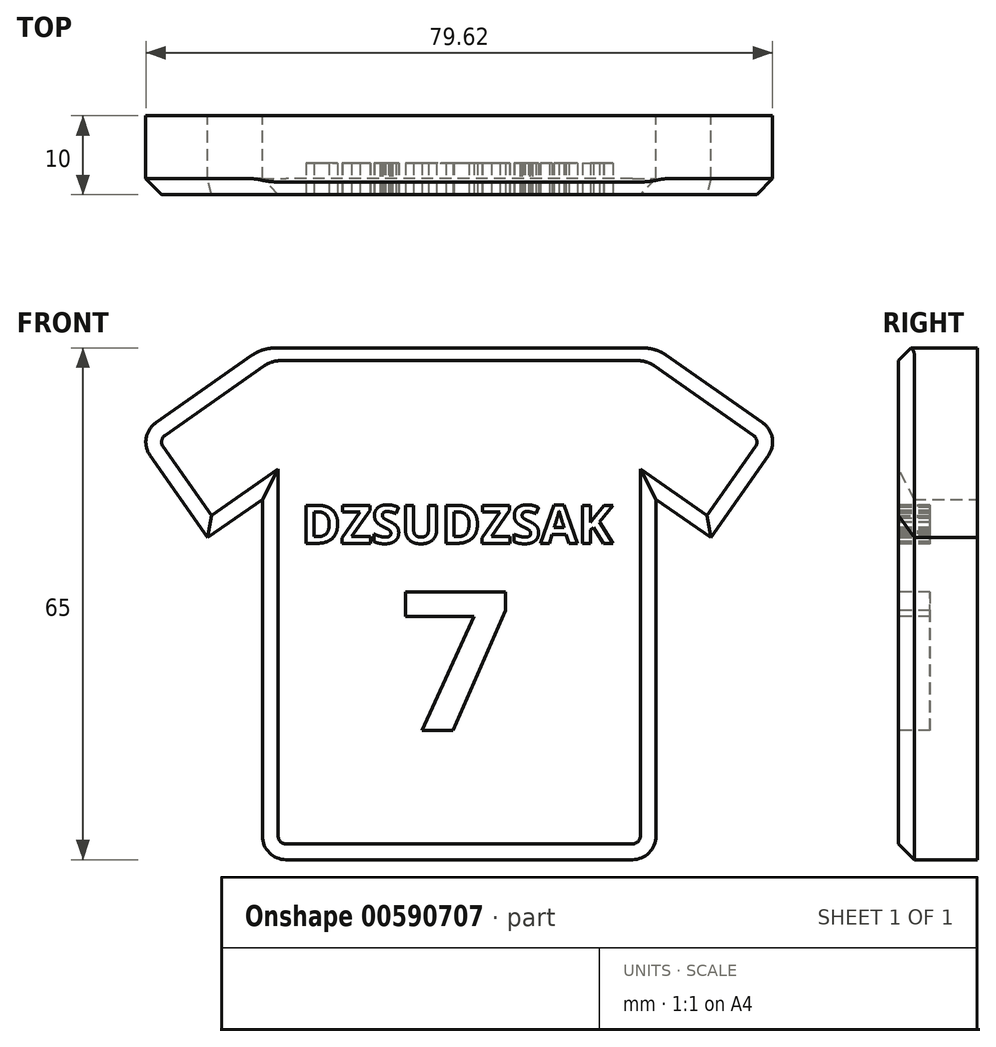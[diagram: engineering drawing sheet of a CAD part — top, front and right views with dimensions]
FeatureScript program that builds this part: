
annotation { "Feature Type Name" : "Feature", "Feature Type Description" : "" }
export const myFeature = defineFeature(function(context is Context, id is Id, definition is map)
    precondition{}
    {
        {
            var Q0;
            Q0=qCreatedBy(makeId("Front.planeOp"),FACE);
            var sketch = newSketch(context, id + "F0", { "sketchPlane" : qUnion([Q0])});
            skLineSegment(sketch, "E0.bottom", {"start": v(0, 36.36) * mm, "end": v(-25, 36.36) * mm});
            skLineSegment(sketch, "E0.top", {"start": v(0, -28.64) * mm, "end": v(-22, -28.64) * mm});
            skLineSegment(sketch, "E0.left", {"start": v(0, 36.36) * mm, "end": v(0, -28.64) * mm});
            skLineSegment(sketch, "E0.right", {"start": v(-25, 36.36) * mm, "end": v(-25, -25.64) * mm});
            skPoint(sketch, "E1.visualSharp", {"position": v(-25, -28.64) * mm});
            skArc(sketch, "E1.filletArc", {"start": v(-25, -25.64) * mm, "mid": v(-24.12, -27.76) * mm, "end": v(-22, -28.64) * mm});
            skArc(sketch, "E2.MirrorCS", {"start": v(25, -25.64) * mm, "mid": v(24.12, -27.76) * mm, "end": v(22, -28.64) * mm});
            skLineSegment(sketch, "E3.MirrorCS", {"start": v(25, 36.36) * mm, "end": v(25, -25.64) * mm});
            skLineSegment(sketch, "E4.MirrorCS", {"start": v(0, 36.36) * mm, "end": v(25, 36.36) * mm});
            skPoint(sketch, "E5.MirrorP", {"position": v(25, -28.64) * mm});
            skLineSegment(sketch, "E6.MirrorCS", {"start": v(0, -28.64) * mm, "end": v(22, -28.64) * mm});
            skLineSegment(sketch, "E7.bottom", {"start": v(25, 36.36) * mm, "end": v(41, 25.16) * mm});
            skLineSegment(sketch, "E7.top", {"start": v(15.98, 23.47) * mm, "end": v(31.97, 12.27) * mm});
            skLineSegment(sketch, "E7.left", {"start": v(25, 36.36) * mm, "end": v(15.98, 23.47) * mm});
            skLineSegment(sketch, "E7.right", {"start": v(41, 25.16) * mm, "end": v(31.97, 12.27) * mm});
            skLineSegment(sketch, "E8.MirrorCS", {"start": v(-25, 36.36) * mm, "end": v(-24.97, 36.32) * mm});
            skPoint(sketch, "E9.orphan", {"position": v(-15.98, 23.47) * mm});
            skLineSegment(sketch, "E10.MirrorCS", {"start": v(-24.97, 36.32) * mm, "end": v(-15.98, 23.47) * mm});
            skLineSegment(sketch, "E11.MirrorCS", {"start": v(-15.98, 23.47) * mm, "end": v(-31.97, 12.27) * mm});
            skLineSegment(sketch, "E12.MirrorCS", {"start": v(-25, 36.36) * mm, "end": v(-41, 25.16) * mm});
            skLineSegment(sketch, "E13", {"start": v(-41, 25.16) * mm, "end": v(-31.97, 12.27) * mm});
            skPoint(sketch, "E14.orphan", {"position": v(-25, 36.36) * mm});
            skSolve(sketch);
        }
        {
            var Q0;
            {var subQ0=sQuery(id+"F0.wireOp",EDGE,"E7.left");Q0=makeQuery(id+"F0.imprint","IMPRINT",FACE,{"disambiguationData":[TD([[makeQuery(id+"F0.imprint","IMPRINT",EDGE,{"derivedFrom":subQ0}),1.0]])]});}
            var Q1;
            {var subQ0=sQuery(id+"F0.wireOp",EDGE,"E7.bottom");Q1=makeQuery(id+"F0.imprint","IMPRINT",FACE,{"disambiguationData":[TD([[makeQuery(id+"F0.imprint","IMPRINT",EDGE,{"derivedFrom":subQ0}),-1.0]])]});}
            var Q2;
            Q2=makeQuery(id+"F0.imprint","IMPRINT",FACE,{"disambiguationData":[TD([[makeQuery(id+"F0.imprint","IMPRINT",EDGE,{"derivedFrom":sQuery(id+"F0.wireOp",EDGE,"E0.left")}),1.0]])]});
            var Q3;
            {var subQ0=sQuery(id+"F0.wireOp",EDGE,"E12.MirrorCS");Q3=makeQuery(id+"F0.imprint","IMPRINT",FACE,{"disambiguationData":[TD([[makeQuery(id+"F0.imprint","IMPRINT",EDGE,{"derivedFrom":subQ0}),1.0]])]});}
            var Q4;
            Q4=makeQuery(id+"F0.imprint","IMPRINT",FACE,{"disambiguationData":[TD([[makeQuery(id+"F0.imprint","IMPRINT",EDGE,{"derivedFrom":sQuery(id+"F0.wireOp",EDGE,"E0.top")}),-1.0]])]});
            var Q5;
            {var subQ0=sQuery(id+"F0.wireOp",EDGE,"961204d5-9f19-48ca-a84b-a6f01696a6780.MirrorCS");var subQ1=sQuery(id+"F0.wireOp",EDGE,"E0.right");var subQ2=makeQuery(id+"F0.imprint","INTERSECT",VERTEX,{"derivedFrom":[subQ1,subQ0]});Q5=makeQuery(id+"F0.imprint","IMPRINT",FACE,{"disambiguationData":[TD([[makeQuery(id+"F0.imprint","IMPRINT",EDGE,{"disambiguationData":[TD([[subQ2,-1.0]])],"derivedFrom":subQ1}),1.0]])]});}
            var Q6;
            {var subQ0=sQuery(id+"F0.wireOp",EDGE,"718d626f-1e87-4561-a077-c9f4c548bd1b0.MirrorCS");Q6=makeQuery(id+"F0.imprint","IMPRINT",FACE,{"disambiguationData":[TD([[makeQuery(id+"F0.imprint","IMPRINT",EDGE,{"derivedFrom":subQ0}),-1.0]])]});}
            var Q7;
            {var subQ1=sQuery(id+"F0.wireOp",EDGE,"E0.bottom");var subQ3=sQuery(id+"F0.wireOp",EDGE,"961204d5-9f19-48ca-a84b-a6f01696a6780.MirrorCS");var subQ4=makeQuery(id+"F0.imprint","INTERSECT",VERTEX,{"derivedFrom":[subQ1,subQ3]});Q7=makeQuery(id+"F0.imprint","IMPRINT",FACE,{"disambiguationData":[TD([[makeQuery(id+"F0.imprint","IMPRINT",EDGE,{"disambiguationData":[TD([[subQ4,-1.0]])],"derivedFrom":subQ3}),-1.0]])]});}
            var Q8;
            {var subQ1=sQuery(id+"F0.wireOp",EDGE,"E0.right");var subQ3=sQuery(id+"F0.wireOp",EDGE,"961204d5-9f19-48ca-a84b-a6f01696a6780.MirrorCS");var subQ4=makeQuery(id+"F0.imprint","INTERSECT",VERTEX,{"derivedFrom":[subQ1,subQ3]});Q8=makeQuery(id+"F0.imprint","IMPRINT",FACE,{"disambiguationData":[TD([[makeQuery(id+"F0.imprint","IMPRINT",EDGE,{"disambiguationData":[TD([[subQ4,1.0]])],"derivedFrom":subQ3}),-1.0]])]});}
            var Q9;
            {var subQ11=sQuery(id+"F0.wireOp",EDGE,"E2.MirrorCS");Q9=makeQuery(id+"F0.imprint","IMPRINT",FACE,{"disambiguationData":[TD([[makeQuery(id+"F0.imprint","IMPRINT",EDGE,{"derivedFrom":subQ11}),-1.0]])]});}
            var Q10;
            {var subQ0=sQuery(id+"F0.wireOp",EDGE,"E8.MirrorCS");Q10=makeQuery(id+"F0.imprint","IMPRINT",FACE,{"disambiguationData":[TD([[makeQuery(id+"F0.imprint","IMPRINT",EDGE,{"derivedFrom":subQ0}),-1.0]])]});}
            extrude(context, id + "F1", {"entities" : qUnion([Q0, Q1, Q2, Q3, Q4, Q5, Q6, Q7, Q8, Q9, Q10]), "depth" : 10 * mm, "offsetDistance" : 25 * mm});
        }
        {
            var Q0;
            Q0=makeQuery(id+"F1.opExtrude","CAP_FACE",FACE,{"disambiguationData":[OSD([sQuery(id+"F0.wireOp",EDGE,"E0.bottom"),sQuery(id+"F0.wireOp",EDGE,"E0.top"),sQuery(id+"F0.wireOp",EDGE,"E0.right"),sQuery(id+"F0.wireOp",EDGE,"E1.filletArc"),sQuery(id+"F0.wireOp",EDGE,"E2.MirrorCS"),sQuery(id+"F0.wireOp",EDGE,"E3.MirrorCS"),sQuery(id+"F0.wireOp",EDGE,"E4.MirrorCS"),sQuery(id+"F0.wireOp",EDGE,"E6.MirrorCS"),sQuery(id+"F0.wireOp",EDGE,"E7.bottom"),sQuery(id+"F0.wireOp",EDGE,"E7.top"),sQuery(id+"F0.wireOp",EDGE,"E7.right"),sQuery(id+"F0.wireOp",EDGE,"961204d5-9f19-48ca-a84b-a6f01696a6780.MirrorCS"),sQuery(id+"F0.wireOp",EDGE,"718d626f-1e87-4561-a077-c9f4c548bd1b0.MirrorCS"),sQuery(id+"F0.wireOp",EDGE,"E11.MirrorCS"),sQuery(id+"F0.wireOp",EDGE,"E12.MirrorCS"),sQuery(id+"F0.wireOp",EDGE,"E13")])],"isStart":false});
            var sketch = newSketch(context, id + "F2", { "sketchPlane" : qUnion([Q0])});
            skText(sketch, "E15", { "text": "DZSUDZSAK", "fontName": "OpenSans-Bold.ttf"});
            skText(sketch, "E16", { "text": "7", "fontName": "OpenSans-Bold.ttf"});
            const initialGuessF2  = {"E15": [-0.02006, 0.01155, 1, 0, 0.00487], "E16": [-0.00746, -0.01222, 1, 0, 0.01779]};
            skSetInitialGuess(sketch, initialGuessF2);
            skSolve(sketch);
        }
        {
            var Q0;
            Q0 = qSketchRegion(id + "F2", true);
            extrude(context, id + "F3", {"entities" : qUnion([Q0]), "operationType" : NewBodyOperationType.REMOVE, "oppositeDirection" : true, "depth" : 4 * mm, "offsetDistance" : 25 * mm});
        }
        {
            var Q0;
            Q0=makeQuery(id+"F1.opExtrude","SWEPT_EDGE",EDGE,{"disambiguationData":[OSD([sQuery(id+"F0.wireOp",EDGE,"E12.MirrorCS"),sQuery(id+"F0.wireOp",EDGE,"E13")])]});
            var Q1;
            Q1=makeQuery(id+"F1.opExtrude","SWEPT_EDGE",EDGE,{"disambiguationData":[OSD([sQuery(id+"F0.wireOp",EDGE,"E7.bottom"),sQuery(id+"F0.wireOp",EDGE,"E7.right")])]});
            fillet(context, id + "F4", {"entities" : qUnion([Q0, Q1]), "radius" : 3 * mm, "tangentPropagation" : true, "allowEdgeOverflow" : false});
        }
        {
            var Q0;
            Q0=makeQuery(id+"F1.opExtrude","CAP_EDGE",EDGE,{"disambiguationData":[OSD([sQuery(id+"F0.wireOp",EDGE,"E12.MirrorCS")])],"isStart":false});
            chamfer(context, id + "F5", {"entities" : qUnion([Q0]), "width" : 2 * mm, "tangentPropagation" : true});
        }
        {
            var Q0;
            Q0=makeQuery(id+"F1.opExtrude","CAP_EDGE",EDGE,{"disambiguationData":[OSD([sQuery(id+"F0.wireOp",EDGE,"E7.bottom")])],"isStart":false});
            var Q1;
            Q1=makeQuery(id+"F1.opExtrude","CAP_EDGE",EDGE,{"disambiguationData":[OSD([sQuery(id+"F0.wireOp",EDGE,"E7.right")])],"isStart":false});
            chamfer(context, id + "F6", {"entities" : qUnion([Q0, Q1]), "width" : 2 * mm, "tangentPropagation" : true});
        }
        {
            var Q0;
            Q0=makeQuery(id+"F1.opExtrude","CAP_EDGE",EDGE,{"disambiguationData":[OSD([sQuery(id+"F0.wireOp",EDGE,"E0.bottom"),sQuery(id+"F0.wireOp",EDGE,"E4.MirrorCS")])],"isStart":false});
            chamfer(context, id + "F7", {"entities" : qUnion([Q0]), "width" : 1.6 * mm, "tangentPropagation" : true});
        }
        {
            var Q0;
            Q0=makeQuery(id+"F1.opExtrude","CAP_EDGE",EDGE,{"disambiguationData":[OSD([sQuery(id+"F0.wireOp",EDGE,"E7.top")])],"isStart":false});
            var Q1;
            Q1=makeQuery(id+"F1.opExtrude","CAP_EDGE",EDGE,{"disambiguationData":[OSD([sQuery(id+"F0.wireOp",EDGE,"E3.MirrorCS")])],"isStart":false});
            var Q2;
            Q2=makeQuery(id+"F1.opExtrude","CAP_EDGE",EDGE,{"disambiguationData":[OSD([sQuery(id+"F0.wireOp",EDGE,"E11.MirrorCS")])],"isStart":false});
            chamfer(context, id + "F8", {"entities" : qUnion([Q0, Q1, Q2]), "width" : 2 * mm, "tangentPropagation" : true});
        }
        {
            var Q0;
            Q0=makeQuery(id+"F1.opExtrude","SWEPT_EDGE",EDGE,{"disambiguationData":[OSD([sQuery(id+"F0.wireOp",EDGE,"E0.bottom"),sQuery(id+"F0.wireOp",EDGE,"E0.right"),sQuery(id+"F0.wireOp",EDGE,"E8.MirrorCS"),sQuery(id+"F0.wireOp",EDGE,"E12.MirrorCS")])]});
            var Q1;
            Q1=makeQuery(id+"F7.opChamfer","BLEND_EDGE",EDGE,{"blendedFrom":[makeQuery(id+"F1.opExtrude","CAP_EDGE",EDGE,{"disambiguationData":[OSD([sQuery(id+"F0.wireOp",EDGE,"E0.bottom"),sQuery(id+"F0.wireOp",EDGE,"E4.MirrorCS")])],"isStart":false}),makeQuery(id+"F5.opChamfer","BLEND_FACE",FACE,{"disambiguationData":[OSD([sQuery(id+"F0.wireOp",EDGE,"E12.MirrorCS")])]})],"blendedInto":[makeQuery(id+"F5.opChamfer","BLEND_FACE",FACE,{"disambiguationData":[OSD([sQuery(id+"F0.wireOp",EDGE,"E12.MirrorCS")])]})]});
            fillet(context, id + "F9", {"entities" : qUnion([Q0, Q1]), "radius" : 5 * mm, "tangentPropagation" : true, "allowEdgeOverflow" : false});
        }
        {
            var Q0;
            Q0=makeQuery(id+"F1.opExtrude","SWEPT_EDGE",EDGE,{"disambiguationData":[OSD([sQuery(id+"F0.wireOp",EDGE,"E3.MirrorCS"),sQuery(id+"F0.wireOp",EDGE,"E4.MirrorCS"),sQuery(id+"F0.wireOp",EDGE,"E7.bottom"),sQuery(id+"F0.wireOp",EDGE,"E7.left")])]});
            var Q1;
            Q1=makeQuery(id+"F7.opChamfer","BLEND_EDGE",EDGE,{"blendedFrom":[makeQuery(id+"F1.opExtrude","CAP_EDGE",EDGE,{"disambiguationData":[OSD([sQuery(id+"F0.wireOp",EDGE,"E0.bottom"),sQuery(id+"F0.wireOp",EDGE,"E4.MirrorCS")])],"isStart":false}),makeQuery(id+"F6.opChamfer","BLEND_FACE",FACE,{"disambiguationData":[OSD([sQuery(id+"F0.wireOp",EDGE,"E7.bottom")])]})],"blendedInto":[makeQuery(id+"F6.opChamfer","BLEND_FACE",FACE,{"disambiguationData":[OSD([sQuery(id+"F0.wireOp",EDGE,"E7.bottom")])]})]});
            fillet(context, id + "F10", {"entities" : qUnion([Q0, Q1]), "radius" : 5 * mm, "tangentPropagation" : true, "allowEdgeOverflow" : false});
        }
    });
